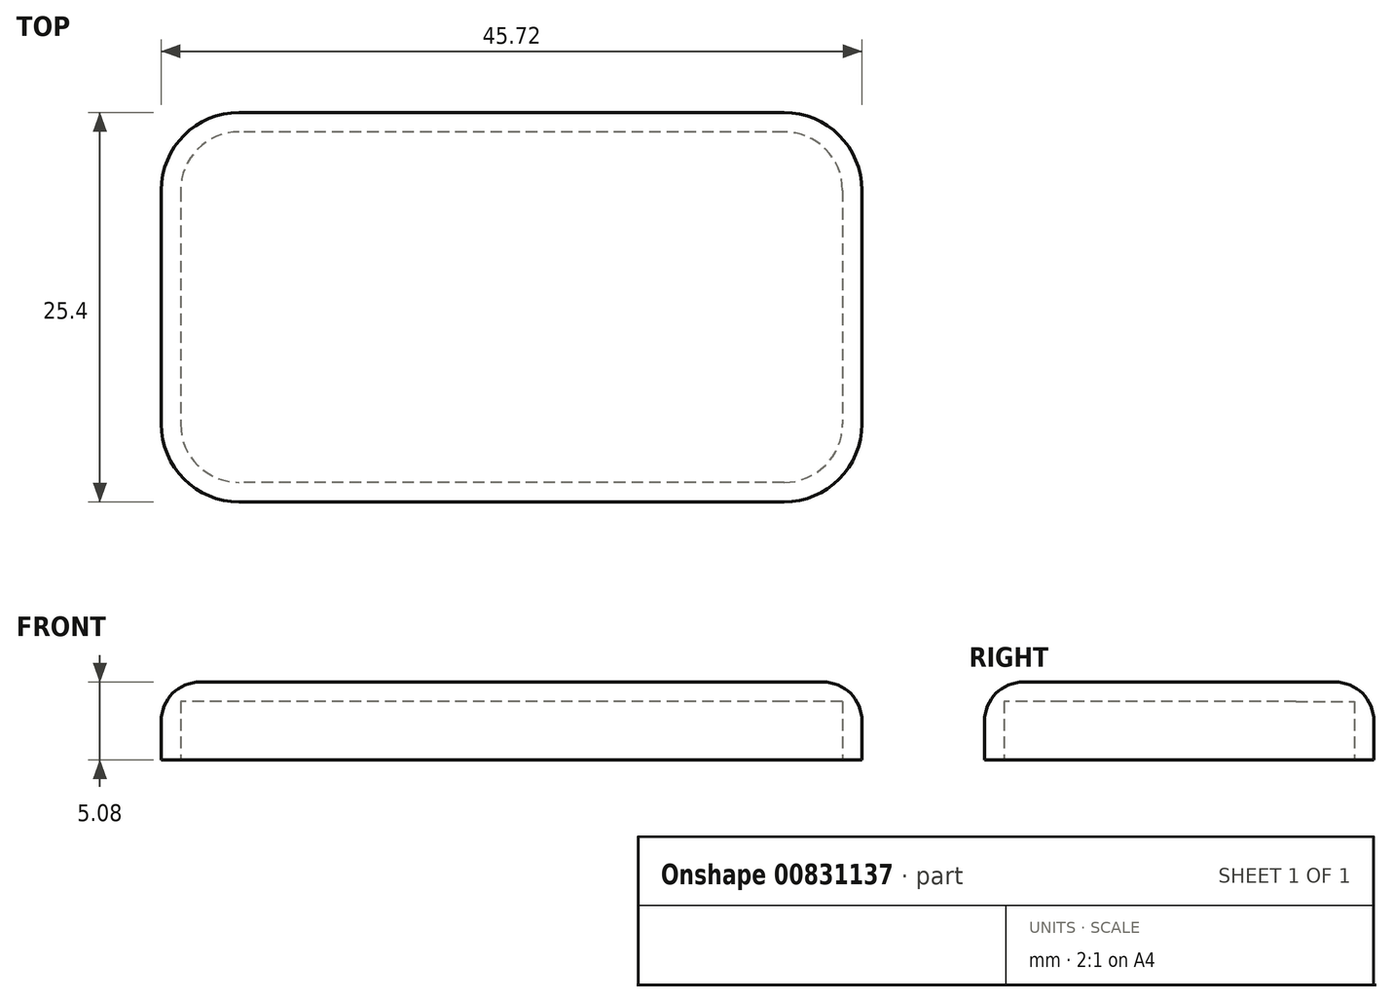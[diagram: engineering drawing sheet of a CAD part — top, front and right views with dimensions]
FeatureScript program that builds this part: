
annotation { "Feature Type Name" : "Feature", "Feature Type Description" : "" }
export const myFeature = defineFeature(function(context is Context, id is Id, definition is map)
    precondition{}
    {
        {
            var Q0;
            Q0=qCreatedBy(makeId("Top.planeOp"),FACE);
            var sketch = newSketch(context, id + "F0", { "sketchPlane" : qUnion([Q0])});
            skLineSegment(sketch, "E0.bottom", {"start": v(17.78, 12.7) * mm, "end": v(-17.78, 12.7) * mm});
            skLineSegment(sketch, "E0.top", {"start": v(17.78, -12.7) * mm, "end": v(-17.78, -12.7) * mm});
            skLineSegment(sketch, "E0.left", {"start": v(22.86, 7.62) * mm, "end": v(22.86, -7.62) * mm});
            skLineSegment(sketch, "E0.right", {"start": v(-22.86, 7.62) * mm, "end": v(-22.86, -7.62) * mm});
            skPoint(sketch, "E0.middle", {"position": v(0, 0) * mm});
            skPoint(sketch, "E1.visualSharp", {"position": v(-22.86, 12.7) * mm});
            skArc(sketch, "E1.filletArc", {"start": v(-17.78, 12.7) * mm, "mid": v(-21.37, 11.21) * mm, "end": v(-22.86, 7.62) * mm});
            skPoint(sketch, "E2.visualSharp", {"position": v(22.86, 12.7) * mm});
            skArc(sketch, "E2.filletArc", {"start": v(22.86, 7.62) * mm, "mid": v(21.37, 11.21) * mm, "end": v(17.78, 12.7) * mm});
            skPoint(sketch, "E3.visualSharp", {"position": v(22.86, -12.7) * mm});
            skArc(sketch, "E3.filletArc", {"start": v(17.78, -12.7) * mm, "mid": v(21.37, -11.21) * mm, "end": v(22.86, -7.62) * mm});
            skPoint(sketch, "E4.visualSharp", {"position": v(-22.86, -12.7) * mm});
            skArc(sketch, "E4.filletArc", {"start": v(-22.86, -7.62) * mm, "mid": v(-21.37, -11.21) * mm, "end": v(-17.78, -12.7) * mm});
            skSolve(sketch);
        }
        {
            var Q0;
            Q0=qSketchRegion(id+"F0",true);
            extrude(context, id + "F1", {"entities" : qUnion([Q0]), "depth" : 5.08 * mm, "offsetDistance" : 25.4 * mm});
        }
        {
            var Q0;
            Q0=makeQuery(id+"F1.opExtrude","CAP_FACE",FACE,{"disambiguationData":[OSD([sQuery(id+"F0.wireOp",EDGE,"E0.bottom"),sQuery(id+"F0.wireOp",EDGE,"E0.top"),sQuery(id+"F0.wireOp",EDGE,"E0.left"),sQuery(id+"F0.wireOp",EDGE,"E0.right"),sQuery(id+"F0.wireOp",EDGE,"E1.filletArc"),sQuery(id+"F0.wireOp",EDGE,"E2.filletArc"),sQuery(id+"F0.wireOp",EDGE,"E3.filletArc"),sQuery(id+"F0.wireOp",EDGE,"E4.filletArc")])],"isStart":true});
            shell(context, id + "F2", {"entities" : qUnion([Q0]), "thickness" : 1.27 * mm});
        }
        {
            var Q0;
            Q0=makeQuery(id+"F1.opExtrude","CAP_EDGE",EDGE,{"disambiguationData":[OSD([sQuery(id+"F0.wireOp",EDGE,"E0.bottom")])],"isStart":false});
            fillet(context, id + "F3", {"entities" : qUnion([Q0]), "radius" : 2.54 * mm, "tangentPropagation" : true, "allowEdgeOverflow" : false});
        }
    });
